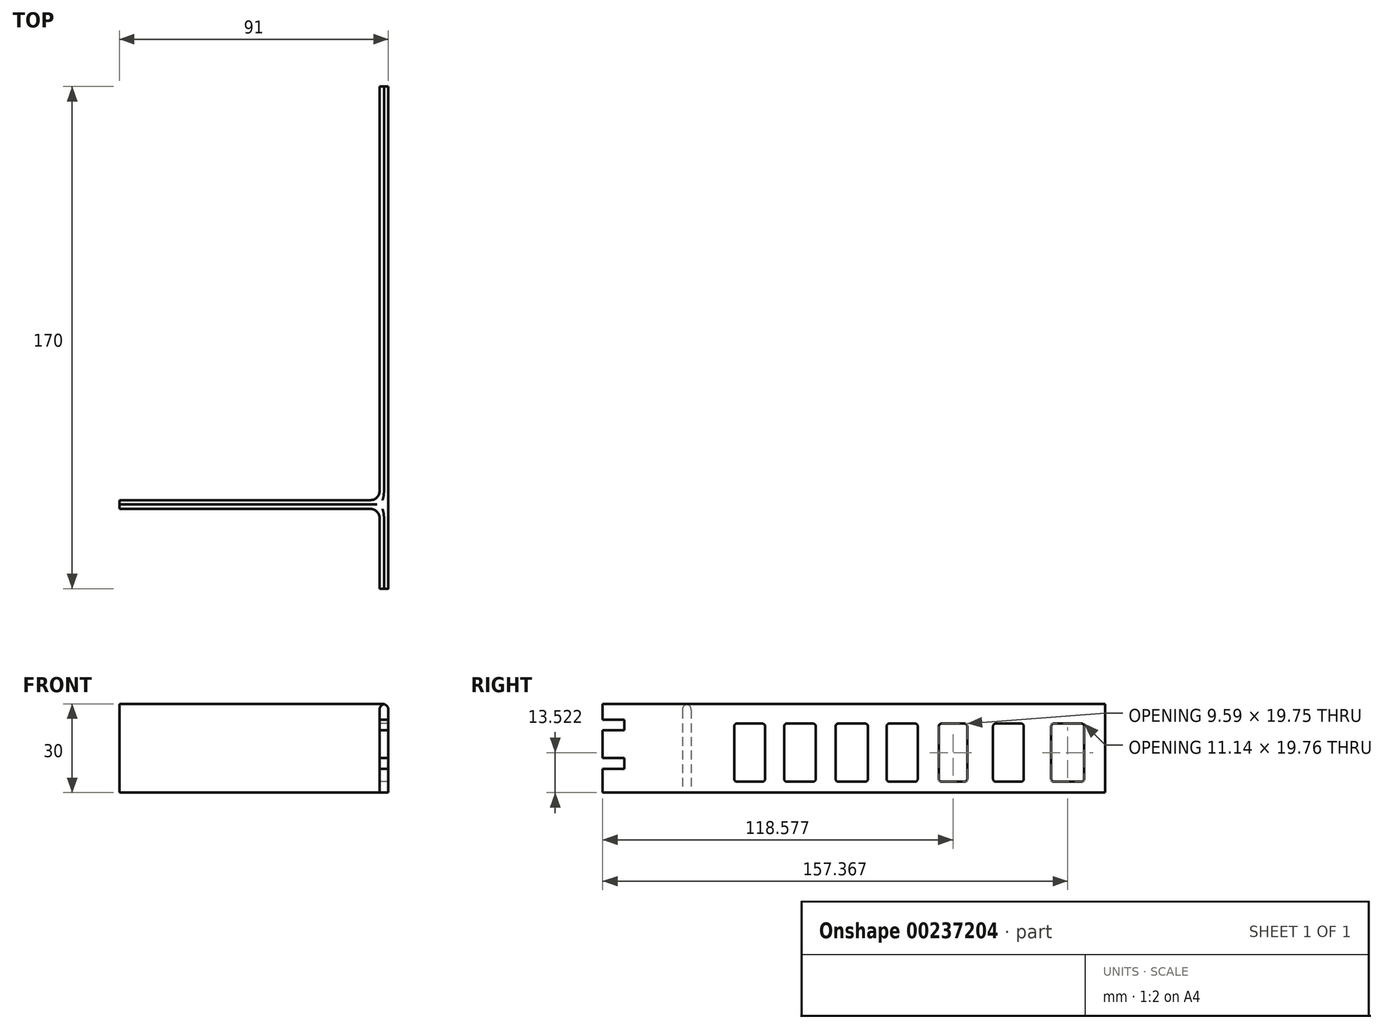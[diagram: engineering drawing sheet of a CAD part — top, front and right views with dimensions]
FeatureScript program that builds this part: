
annotation { "Feature Type Name" : "Feature", "Feature Type Description" : "" }
export const myFeature = defineFeature(function(context is Context, id is Id, definition is map)
    precondition{}
    {
        {
            var Q0;
            Q0=qCreatedBy(makeId("Top.planeOp"),FACE);
            var sketch = newSketch(context, id + "F0", { "sketchPlane" : qUnion([Q0])});
            skLineSegment(sketch, "E0", {"start": v(0, 0) * mm, "end": v(0, -140) * mm});
            skLineSegment(sketch, "E1", {"start": v(0, -140) * mm, "end": v(-88, -140) * mm});
            skLineSegment(sketch, "E2", {"start": v(0, -140) * mm, "end": v(0, -170) * mm});
            skLineSegment(sketch, "E3.0", {"start": v(3, 0) * mm, "end": v(3, -140) * mm});
            skLineSegment(sketch, "E4.0", {"start": v(3, -140) * mm, "end": v(3, -170) * mm});
            skLineSegment(sketch, "E5.0", {"start": v(0, -143) * mm, "end": v(-88, -143) * mm});
            skLineSegment(sketch, "E6", {"start": v(0, -170) * mm, "end": v(3, -170) * mm});
            skLineSegment(sketch, "E7", {"start": v(0, 0) * mm, "end": v(3, 0) * mm});
            skLineSegment(sketch, "E8", {"start": v(-88, -143) * mm, "end": v(-88, -140) * mm});
            skSolve(sketch);
        }
        {
            var Q0;
            Q0 = qSketchRegion(id + "F0", true);
            extrude(context, id + "F1", {"entities" : qUnion([Q0]), "depth" : 30 * mm});
        }
        {
            var Q0;
            Q0=makeQuery(id+"F1.opExtrude","SWEPT_EDGE",EDGE,{"disambiguationData":[OSD([sQuery(id+"F0.wireOp",EDGE,"E0"),sQuery(id+"F0.wireOp",EDGE,"E1"),sQuery(id+"F0.wireOp",EDGE,"E2")])]});
            var Q1;
            Q1=makeQuery(id+"F1.opExtrude","SWEPT_EDGE",EDGE,{"disambiguationData":[OSD([sQuery(id+"F0.wireOp",EDGE,"E2"),sQuery(id+"F0.wireOp",EDGE,"E5.0")])]});
            fillet(context, id + "F2", {"entities" : qUnion([Q0, Q1]), "radius" : 3 * mm, "tangentPropagation" : true, "allowEdgeOverflow" : false});
        }
        {
            var Q0;
            Q0=makeQuery(id+"F1.opExtrude","CAP_EDGE",EDGE,{"disambiguationData":[OSD([sQuery(id+"F0.wireOp",EDGE,"E0")])],"isStart":false});
            var Q1;
            Q1=makeQuery(id+"F1.opExtrude","CAP_EDGE",EDGE,{"disambiguationData":[OSD([sQuery(id+"F0.wireOp",EDGE,"E5.0")])],"isStart":false});
            var Q2;
            Q2=makeQuery(id+"F1.opExtrude","CAP_EDGE",EDGE,{"disambiguationData":[OSD([sQuery(id+"F0.wireOp",EDGE,"E3.0"),sQuery(id+"F0.wireOp",EDGE,"E4.0")])],"isStart":false});
            fillet(context, id + "F3", {"entities" : qUnion([Q0, Q1, Q2]), "radius" : 2 * mm, "tangentPropagation" : true, "allowEdgeOverflow" : false});
        }
        {
            var Q0;
            Q0=makeQuery(id+"F1.opExtrude","SWEPT_FACE",FACE,{"disambiguationData":[OSD([sQuery(id+"F0.wireOp",EDGE,"E2")])]});
            var sketch = newSketch(context, id + "F4", { "sketchPlane" : qUnion([Q0])});
            skLineSegment(sketch, "E9.bottom", {"start": v(170, 24.7) * mm, "end": v(162.6, 24.7) * mm});
            skLineSegment(sketch, "E9.top", {"start": v(170, 21.07) * mm, "end": v(162.6, 21.07) * mm});
            skLineSegment(sketch, "E9.left", {"start": v(170, 24.7) * mm, "end": v(170, 21.07) * mm});
            skLineSegment(sketch, "E9.right", {"start": v(162.6, 24.7) * mm, "end": v(162.6, 21.07) * mm});
            skLineSegment(sketch, "E10.bottom", {"start": v(170, 11.68) * mm, "end": v(162.6, 11.68) * mm});
            skLineSegment(sketch, "E10.top", {"start": v(170, 7.97) * mm, "end": v(162.6, 7.97) * mm});
            skLineSegment(sketch, "E10.left", {"start": v(170, 11.68) * mm, "end": v(170, 7.97) * mm});
            skLineSegment(sketch, "E10.right", {"start": v(162.6, 11.68) * mm, "end": v(162.6, 7.97) * mm});
            skSolve(sketch);
        }
        {
            var Q0;
            Q0=makeQuery(id+"F4.imprint","IMPRINT",FACE,{"disambiguationData":[TD([[makeQuery(id+"F4.imprint","IMPRINT",EDGE,{"derivedFrom":sQuery(id+"F4.wireOp",EDGE,"E9.bottom")}),1.0]])]});
            var Q1;
            Q1=makeQuery(id+"F4.imprint","IMPRINT",FACE,{"disambiguationData":[TD([[makeQuery(id+"F4.imprint","IMPRINT",EDGE,{"derivedFrom":sQuery(id+"F4.wireOp",EDGE,"E10.bottom")}),1.0]])]});
            extrude(context, id + "F5", {"entities" : qUnion([Q0, Q1]), "operationType" : NewBodyOperationType.REMOVE, "oppositeDirection" : true, "depth" : 3 * mm});
        }
        {
            var Q0;
            Q0=makeQuery(id+"F1.opExtrude","SWEPT_FACE",FACE,{"disambiguationData":[OSD([sQuery(id+"F0.wireOp",EDGE,"E0")])]});
            var sketch = newSketch(context, id + "F6", { "sketchPlane" : qUnion([Q0])});
            skLineSegment(sketch, "E11.bottom", {"start": v(7.06, 23.4) * mm, "end": v(18.2, 23.4) * mm});
            skLineSegment(sketch, "E11.top", {"start": v(7.06, 3.64) * mm, "end": v(18.2, 3.64) * mm});
            skLineSegment(sketch, "E11.left", {"start": v(7.06, 23.4) * mm, "end": v(7.06, 3.64) * mm});
            skLineSegment(sketch, "E11.right", {"start": v(18.2, 23.4) * mm, "end": v(18.2, 3.64) * mm});
            skLineSegment(sketch, "E12.bottom", {"start": v(27.48, 23.4) * mm, "end": v(37.89, 23.4) * mm});
            skLineSegment(sketch, "E12.top", {"start": v(27.48, 3.64) * mm, "end": v(37.89, 3.64) * mm});
            skLineSegment(sketch, "E12.left", {"start": v(27.48, 23.4) * mm, "end": v(27.48, 3.64) * mm});
            skLineSegment(sketch, "E12.right", {"start": v(37.89, 23.4) * mm, "end": v(37.89, 3.64) * mm});
            skLineSegment(sketch, "E13.bottom", {"start": v(46.63, 23.4) * mm, "end": v(56.22, 23.4) * mm});
            skLineSegment(sketch, "E13.top", {"start": v(46.63, 3.64) * mm, "end": v(56.22, 3.64) * mm});
            skLineSegment(sketch, "E13.left", {"start": v(46.63, 23.4) * mm, "end": v(46.63, 3.64) * mm});
            skLineSegment(sketch, "E13.right", {"start": v(56.22, 23.4) * mm, "end": v(56.22, 3.64) * mm});
            skLineSegment(sketch, "E14.bottom", {"start": v(63.36, 23.4) * mm, "end": v(73.9, 23.4) * mm});
            skLineSegment(sketch, "E14.top", {"start": v(63.36, 3.64) * mm, "end": v(73.9, 3.64) * mm});
            skLineSegment(sketch, "E14.left", {"start": v(63.36, 23.4) * mm, "end": v(63.36, 3.64) * mm});
            skLineSegment(sketch, "E14.right", {"start": v(73.9, 23.4) * mm, "end": v(73.9, 3.64) * mm});
            skLineSegment(sketch, "E15.bottom", {"start": v(80.23, 23.4) * mm, "end": v(91.15, 23.4) * mm});
            skLineSegment(sketch, "E15.top", {"start": v(80.23, 3.64) * mm, "end": v(91.15, 3.64) * mm});
            skLineSegment(sketch, "E15.left", {"start": v(80.23, 23.4) * mm, "end": v(80.23, 3.64) * mm});
            skLineSegment(sketch, "E15.right", {"start": v(91.15, 23.4) * mm, "end": v(91.15, 3.64) * mm});
            skLineSegment(sketch, "E16.bottom", {"start": v(97.9, 23.4) * mm, "end": v(108.56, 23.4) * mm});
            skLineSegment(sketch, "E16.top", {"start": v(97.9, 3.64) * mm, "end": v(108.56, 3.64) * mm});
            skLineSegment(sketch, "E16.left", {"start": v(97.9, 23.4) * mm, "end": v(97.9, 3.64) * mm});
            skLineSegment(sketch, "E16.right", {"start": v(108.56, 23.4) * mm, "end": v(108.56, 3.64) * mm});
            skLineSegment(sketch, "E17.bottom", {"start": v(115.04, 23.4) * mm, "end": v(125.46, 23.4) * mm});
            skLineSegment(sketch, "E17.top", {"start": v(115.04, 3.64) * mm, "end": v(125.46, 3.64) * mm});
            skLineSegment(sketch, "E17.left", {"start": v(115.04, 23.4) * mm, "end": v(115.04, 3.64) * mm});
            skLineSegment(sketch, "E17.right", {"start": v(125.46, 23.4) * mm, "end": v(125.46, 3.64) * mm});
            skSolve(sketch);
        }
        {
            var Q0;
            Q0 = qSketchRegion(id + "F6", true);
            extrude(context, id + "F7", {"entities" : qUnion([Q0]), "operationType" : NewBodyOperationType.REMOVE, "oppositeDirection" : true, "depth" : 3 * mm});
        }
        {
            var Q0;
            Q0=makeQuery(id+"F7.boolean.opBoolean","COPY",EDGE,{"derivedFrom":makeQuery(id+"F7.opExtrude","SWEPT_EDGE",EDGE,{"disambiguationData":[OSD([sQuery(id+"F6.wireOp",EDGE,"E11.bottom"),sQuery(id+"F6.wireOp",EDGE,"E11.left")])]})});
            var Q1;
            Q1=makeQuery(id+"F7.boolean.opBoolean","COPY",EDGE,{"derivedFrom":makeQuery(id+"F7.opExtrude","SWEPT_EDGE",EDGE,{"disambiguationData":[OSD([sQuery(id+"F6.wireOp",EDGE,"E12.bottom"),sQuery(id+"F6.wireOp",EDGE,"E12.left")])]})});
            var Q2;
            Q2=makeQuery(id+"F7.boolean.opBoolean","COPY",EDGE,{"derivedFrom":makeQuery(id+"F7.opExtrude","SWEPT_EDGE",EDGE,{"disambiguationData":[OSD([sQuery(id+"F6.wireOp",EDGE,"E13.bottom"),sQuery(id+"F6.wireOp",EDGE,"E13.left")])]})});
            var Q3;
            Q3=makeQuery(id+"F7.boolean.opBoolean","COPY",EDGE,{"derivedFrom":makeQuery(id+"F7.opExtrude","SWEPT_EDGE",EDGE,{"disambiguationData":[OSD([sQuery(id+"F6.wireOp",EDGE,"E14.bottom"),sQuery(id+"F6.wireOp",EDGE,"E14.left")])]})});
            var Q4;
            Q4=makeQuery(id+"F7.boolean.opBoolean","COPY",EDGE,{"derivedFrom":makeQuery(id+"F7.opExtrude","SWEPT_EDGE",EDGE,{"disambiguationData":[OSD([sQuery(id+"F6.wireOp",EDGE,"E15.bottom"),sQuery(id+"F6.wireOp",EDGE,"E15.left")])]})});
            var Q5;
            Q5=makeQuery(id+"F7.boolean.opBoolean","COPY",EDGE,{"derivedFrom":makeQuery(id+"F7.opExtrude","SWEPT_EDGE",EDGE,{"disambiguationData":[OSD([sQuery(id+"F6.wireOp",EDGE,"E16.bottom"),sQuery(id+"F6.wireOp",EDGE,"E16.left")])]})});
            var Q6;
            Q6=makeQuery(id+"F7.boolean.opBoolean","COPY",EDGE,{"derivedFrom":makeQuery(id+"F7.opExtrude","SWEPT_EDGE",EDGE,{"disambiguationData":[OSD([sQuery(id+"F6.wireOp",EDGE,"E17.bottom"),sQuery(id+"F6.wireOp",EDGE,"E17.left")])]})});
            var Q7;
            Q7=makeQuery(id+"F7.boolean.opBoolean","COPY",EDGE,{"derivedFrom":makeQuery(id+"F7.opExtrude","SWEPT_EDGE",EDGE,{"disambiguationData":[OSD([sQuery(id+"F6.wireOp",EDGE,"E11.top"),sQuery(id+"F6.wireOp",EDGE,"E11.left")])]})});
            var Q8;
            Q8=makeQuery(id+"F7.boolean.opBoolean","COPY",EDGE,{"derivedFrom":makeQuery(id+"F7.opExtrude","SWEPT_EDGE",EDGE,{"disambiguationData":[OSD([sQuery(id+"F6.wireOp",EDGE,"E12.top"),sQuery(id+"F6.wireOp",EDGE,"E12.left")])]})});
            var Q9;
            Q9=makeQuery(id+"F7.boolean.opBoolean","COPY",EDGE,{"derivedFrom":makeQuery(id+"F7.opExtrude","SWEPT_EDGE",EDGE,{"disambiguationData":[OSD([sQuery(id+"F6.wireOp",EDGE,"E13.top"),sQuery(id+"F6.wireOp",EDGE,"E13.left")])]})});
            var Q10;
            Q10=makeQuery(id+"F7.boolean.opBoolean","COPY",EDGE,{"derivedFrom":makeQuery(id+"F7.opExtrude","SWEPT_EDGE",EDGE,{"disambiguationData":[OSD([sQuery(id+"F6.wireOp",EDGE,"E14.top"),sQuery(id+"F6.wireOp",EDGE,"E14.left")])]})});
            var Q11;
            Q11=makeQuery(id+"F7.boolean.opBoolean","COPY",EDGE,{"derivedFrom":makeQuery(id+"F7.opExtrude","SWEPT_EDGE",EDGE,{"disambiguationData":[OSD([sQuery(id+"F6.wireOp",EDGE,"E15.top"),sQuery(id+"F6.wireOp",EDGE,"E15.left")])]})});
            var Q12;
            Q12=makeQuery(id+"F7.boolean.opBoolean","COPY",EDGE,{"derivedFrom":makeQuery(id+"F7.opExtrude","SWEPT_EDGE",EDGE,{"disambiguationData":[OSD([sQuery(id+"F6.wireOp",EDGE,"E16.top"),sQuery(id+"F6.wireOp",EDGE,"E16.left")])]})});
            var Q13;
            Q13=makeQuery(id+"F7.boolean.opBoolean","COPY",EDGE,{"derivedFrom":makeQuery(id+"F7.opExtrude","SWEPT_EDGE",EDGE,{"disambiguationData":[OSD([sQuery(id+"F6.wireOp",EDGE,"E17.top"),sQuery(id+"F6.wireOp",EDGE,"E17.left")])]})});
            var Q14;
            Q14=makeQuery(id+"F7.boolean.opBoolean","COPY",EDGE,{"derivedFrom":makeQuery(id+"F7.opExtrude","SWEPT_EDGE",EDGE,{"disambiguationData":[OSD([sQuery(id+"F6.wireOp",EDGE,"E17.bottom"),sQuery(id+"F6.wireOp",EDGE,"E17.right")])]})});
            var Q15;
            Q15=makeQuery(id+"F7.boolean.opBoolean","COPY",EDGE,{"derivedFrom":makeQuery(id+"F7.opExtrude","SWEPT_EDGE",EDGE,{"disambiguationData":[OSD([sQuery(id+"F6.wireOp",EDGE,"E16.bottom"),sQuery(id+"F6.wireOp",EDGE,"E16.right")])]})});
            var Q16;
            Q16=makeQuery(id+"F7.boolean.opBoolean","COPY",EDGE,{"derivedFrom":makeQuery(id+"F7.opExtrude","SWEPT_EDGE",EDGE,{"disambiguationData":[OSD([sQuery(id+"F6.wireOp",EDGE,"E15.bottom"),sQuery(id+"F6.wireOp",EDGE,"E15.right")])]})});
            var Q17;
            Q17=makeQuery(id+"F7.boolean.opBoolean","COPY",EDGE,{"derivedFrom":makeQuery(id+"F7.opExtrude","SWEPT_EDGE",EDGE,{"disambiguationData":[OSD([sQuery(id+"F6.wireOp",EDGE,"E14.bottom"),sQuery(id+"F6.wireOp",EDGE,"E14.right")])]})});
            var Q18;
            Q18=makeQuery(id+"F7.boolean.opBoolean","COPY",EDGE,{"derivedFrom":makeQuery(id+"F7.opExtrude","SWEPT_EDGE",EDGE,{"disambiguationData":[OSD([sQuery(id+"F6.wireOp",EDGE,"E13.bottom"),sQuery(id+"F6.wireOp",EDGE,"E13.right")])]})});
            var Q19;
            Q19=makeQuery(id+"F7.boolean.opBoolean","COPY",EDGE,{"derivedFrom":makeQuery(id+"F7.opExtrude","SWEPT_EDGE",EDGE,{"disambiguationData":[OSD([sQuery(id+"F6.wireOp",EDGE,"E12.bottom"),sQuery(id+"F6.wireOp",EDGE,"E12.right")])]})});
            var Q20;
            Q20=makeQuery(id+"F7.boolean.opBoolean","COPY",EDGE,{"derivedFrom":makeQuery(id+"F7.opExtrude","SWEPT_EDGE",EDGE,{"disambiguationData":[OSD([sQuery(id+"F6.wireOp",EDGE,"E11.bottom"),sQuery(id+"F6.wireOp",EDGE,"E11.right")])]})});
            var Q21;
            Q21=makeQuery(id+"F7.boolean.opBoolean","COPY",EDGE,{"derivedFrom":makeQuery(id+"F7.opExtrude","SWEPT_EDGE",EDGE,{"disambiguationData":[OSD([sQuery(id+"F6.wireOp",EDGE,"E11.top"),sQuery(id+"F6.wireOp",EDGE,"E11.right")])]})});
            var Q22;
            Q22=makeQuery(id+"F7.boolean.opBoolean","COPY",EDGE,{"derivedFrom":makeQuery(id+"F7.opExtrude","SWEPT_EDGE",EDGE,{"disambiguationData":[OSD([sQuery(id+"F6.wireOp",EDGE,"E12.top"),sQuery(id+"F6.wireOp",EDGE,"E12.right")])]})});
            var Q23;
            Q23=makeQuery(id+"F7.boolean.opBoolean","COPY",EDGE,{"derivedFrom":makeQuery(id+"F7.opExtrude","SWEPT_EDGE",EDGE,{"disambiguationData":[OSD([sQuery(id+"F6.wireOp",EDGE,"E13.top"),sQuery(id+"F6.wireOp",EDGE,"E13.right")])]})});
            var Q24;
            Q24=makeQuery(id+"F7.boolean.opBoolean","COPY",EDGE,{"derivedFrom":makeQuery(id+"F7.opExtrude","SWEPT_EDGE",EDGE,{"disambiguationData":[OSD([sQuery(id+"F6.wireOp",EDGE,"E14.top"),sQuery(id+"F6.wireOp",EDGE,"E14.right")])]})});
            var Q25;
            Q25=makeQuery(id+"F7.boolean.opBoolean","COPY",EDGE,{"derivedFrom":makeQuery(id+"F7.opExtrude","SWEPT_EDGE",EDGE,{"disambiguationData":[OSD([sQuery(id+"F6.wireOp",EDGE,"E15.top"),sQuery(id+"F6.wireOp",EDGE,"E15.right")])]})});
            var Q26;
            Q26=makeQuery(id+"F7.boolean.opBoolean","COPY",EDGE,{"derivedFrom":makeQuery(id+"F7.opExtrude","SWEPT_EDGE",EDGE,{"disambiguationData":[OSD([sQuery(id+"F6.wireOp",EDGE,"E16.top"),sQuery(id+"F6.wireOp",EDGE,"E16.right")])]})});
            var Q27;
            Q27=makeQuery(id+"F7.boolean.opBoolean","COPY",EDGE,{"derivedFrom":makeQuery(id+"F7.opExtrude","SWEPT_EDGE",EDGE,{"disambiguationData":[OSD([sQuery(id+"F6.wireOp",EDGE,"E17.top"),sQuery(id+"F6.wireOp",EDGE,"E17.right")])]})});
            fillet(context, id + "F8", {"entities" : qUnion([Q0, Q1, Q2, Q3, Q4, Q5, Q6, Q7, Q8, Q9, Q10, Q11, Q12, Q13, Q14, Q15, Q16, Q17, Q18, Q19, Q20, Q21, Q22, Q23, Q24, Q25, Q26, Q27]), "radius" : 1 * mm, "tangentPropagation" : true, "allowEdgeOverflow" : false});
        }
    });
